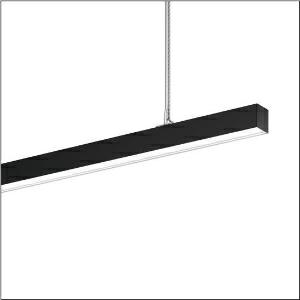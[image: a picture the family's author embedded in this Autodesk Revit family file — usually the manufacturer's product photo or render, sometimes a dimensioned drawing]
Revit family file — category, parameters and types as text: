
# Revit family: silica_r__21_51mx33db49bb_8fe2
name_source: partatom
category: Lighting Fixtures
units: mm (PartAtom-declared; Revit-internal decimal feet)

## family parameters
Cut with Voids When Loaded = No
Host = Face
Light Source = No
Part Type = Normal
Room Calculation Point = No
Round Connector Dimension = Use Diameter
Shared = No

## types (1)
- --- (1 x LED, 7390 lm, 48.3 W, 4000K)
    Apparent Load = 48 VA
    CIE Flux Codes = 78 96 99 55 100
    Color Rendering = 80
    Color Temperature = 4000K
    Default Elevation = 1800 mm
    Description = Silica® 21, office luminaire, primary optical cover: prismatic diffuser, of PMMA, CAT 2 (L<= 3000cd/m²), light emission: direct/indirect distribution, primary light characteristic: symmetric, installation type: suspended mounting, LED, rated luminous flux: 7.390lm, luminous efficacy: 153lm/W, light colour: 840, colour temperature: 4000K, with terminal, 3+2-pole, max. 2.5mm², mains connection: 220..240V, AC, 50/60Hz, rated input power: 48.3W, luminaire housing, of aluminium, jet black (RAL 9005), length: 1.504mm, width: 53mm, height: 53mm, protection rating (complete): IP20, insulation class (complete): insulation class I (protective earthing), certification: CE, permissible operating ambient temperature: 0..+35°C, standard: EN 50419, packaging unit: 1 piece
    Height = 53 mm
    Lamp = 1 x LED
    Lamp Light Flux = 7390 lm
    Lamp Power = 48.3 W
    Lamp count = 1
    Length = 1504 mm
    Luminous efficacy = 153 lm/W
    Manufacturer = Siteco
    ModVariant = No
    Model = 51MX33DB49BB
    Mounting Place = Ceiling
    Mounting Type = Pendant
    Number of Poles = 1
    OnlyDefault = Yes
    Power Factor = 1
    Product Name = Silica® 21
    Product group = office luminaire | ceiling pendant
    ProductGroupID = 902
    Protection Class = Protection class I
    Protection Degree = IP 20
    RLX_Detail_Level = 1
    RLX_Emergency_Light_Flux = 0 lm
    RLX_Emergency_Type = 0
    RLX_Emergency_Type_DB = No
    RlxData = <blob elided: 26145 chars, md5=9657da59>
    Socket = socket
    Standby Power = 0 W
    System Light Flux = 7390 lm
    System Power = 48 W
    Type Comments = factory setting: luminous flux: 100 % | dim-lin: 254 | 323 mA
    Type Image = l_1297744.jpg
    URL = http://relux.com
    VarID = @adj_048779
    Voltage = 0 V
    Weight = 0.00 kg
    Width = 53 mm

## geometry (parser evidence)
native form markers: Blend x4, Sweep x14
no freeform markers — native parametric forms only
